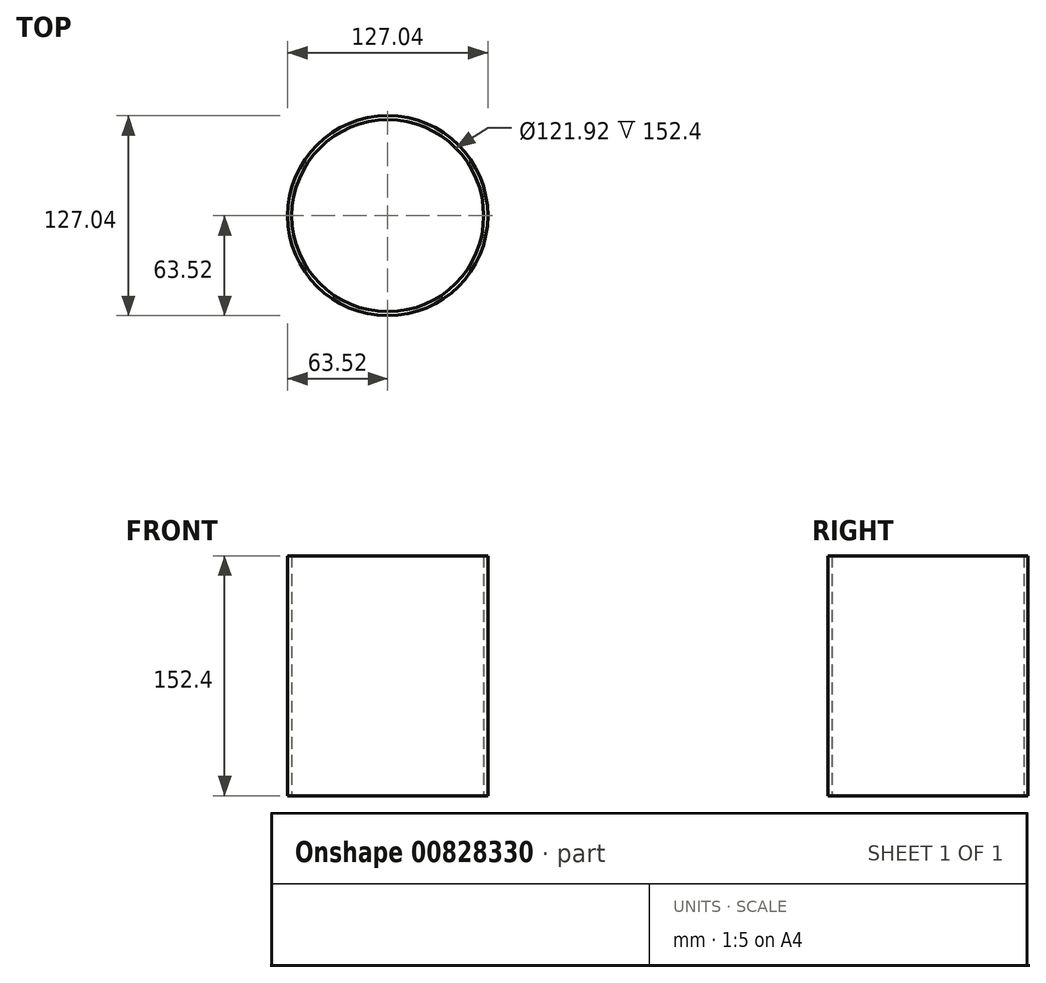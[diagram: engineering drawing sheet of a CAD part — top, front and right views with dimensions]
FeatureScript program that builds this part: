
annotation { "Feature Type Name" : "Feature", "Feature Type Description" : "" }
export const myFeature = defineFeature(function(context is Context, id is Id, definition is map)
    precondition{}
    {
        {
            var Q0;
            Q0=qCreatedBy(makeId("Top.planeOp"),FACE);
            var sketch = newSketch(context, id + "F0", { "sketchPlane" : qUnion([Q0])});
            skCircle(sketch, "E0", {"center": v(0, 0) * mm, "radius": 63.52 * mm});
            skSolve(sketch);
        }
        {
            var Q0;
            Q0=makeQuery(id+"F0.imprint","IMPRINT",FACE,{"disambiguationData":[TD([[makeQuery(id+"F0.imprint","IMPRINT",EDGE,{"derivedFrom":sQuery(id+"F0.wireOp",EDGE,"E0")}),1.0]])]});
            extrude(context, id + "F1", {"entities" : qUnion([Q0]), "depth" : 152.4 * mm, "offsetDistance" : 25.4 * mm});
        }
        {
            var Q0;
            Q0=makeQuery(id+"F1.opExtrude","CAP_FACE",FACE,{"disambiguationData":[OSD([sQuery(id+"F0.wireOp",EDGE,"E0")])],"isStart":true});
            var sketch = newSketch(context, id + "F2", { "sketchPlane" : qUnion([Q0])});
            skCircle(sketch, "E1", {"center": v(0, 0) * mm, "radius": 60.5 * mm});
            skSolve(sketch);
        }
        {
            var Q0;
            Q0=sQuery(id+"F2.wireOp",VERTEX,"E1.center");
            var Q1;
            Q1=makeQuery(id+"F1.opExtrude","SWEPT_BODY",BODY,{"disambiguationData":[OSD([sQuery(id+"F0.wireOp",EDGE,"E0")])]});
            hole(context, id + "F3", {"style" : HoleStyle.SIMPLE, "endStyle" : HoleEndStyle.THROUGH, "holeDiameter" : 121.92 * mm, "majorDiameter" : 6.35 * mm, "isTappedThrough" : true, "tappedDepth" : 12.7 * mm, "tapClearance" : 3, "locations" : qUnion([Q0]), "scope" : qUnion([Q1])});
        }
    });
